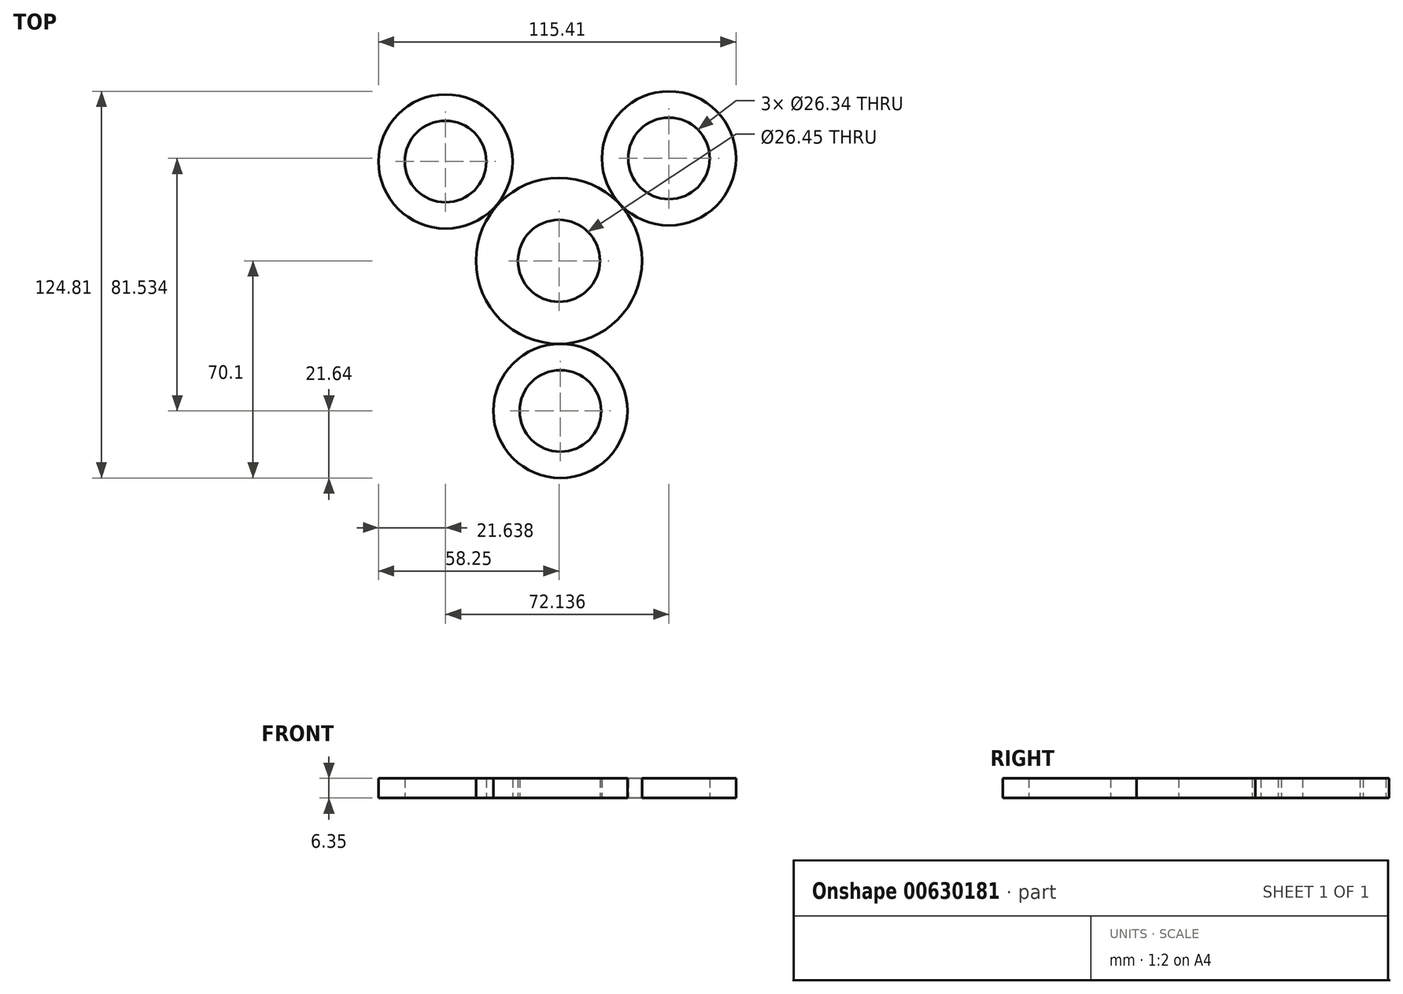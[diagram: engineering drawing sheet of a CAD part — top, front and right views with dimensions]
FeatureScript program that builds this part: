
annotation { "Feature Type Name" : "Feature", "Feature Type Description" : "" }
export const myFeature = defineFeature(function(context is Context, id is Id, definition is map)
    precondition{}
    {
        {
            var Q0;
            Q0=qCreatedBy(makeId("Top.planeOp"),FACE);
            var sketch = newSketch(context, id + "F0", { "sketchPlane" : qUnion([Q0])});
            skCircle(sketch, "E0", {"center": v(0, 0) * mm, "radius": 13.23 * mm});
            skSolve(sketch);
        }
        {
            var Q0;
            Q0=makeQuery(id+"F0.imprint","IMPRINT",FACE,{"disambiguationData":[TD([[makeQuery(id+"F0.imprint","IMPRINT",EDGE,{"derivedFrom":sQuery(id+"F0.wireOp",EDGE,"E0")}),1.0]])]});
            var sketch = newSketch(context, id + "F1", { "sketchPlane" : qUnion([Q0])});
            skCircle(sketch, "E1", {"center": v(0, 0) * mm, "radius": 26.8 * mm});
            skSolve(sketch);
        }
        {
            var Q0;
            Q0=makeQuery(id+"F1.imprint","IMPRINT",FACE,{"disambiguationData":[TD([[makeQuery(id+"F1.imprint","IMPRINT",EDGE,{"derivedFrom":sQuery(id+"F1.wireOp",EDGE,"E1")}),1.0]])]});
            extrude(context, id + "F2", {"entities" : qUnion([Q0]), "depth" : 6.35 * mm, "offsetDistance" : 25.4 * mm});
        }
        {
            var Q0;
            Q0=qCreatedBy(makeId("Top.planeOp"),FACE);
            var sketch = newSketch(context, id + "F3", { "sketchPlane" : qUnion([Q0])});
            skCircle(sketch, "E2", {"center": v(-36.61, 32.06) * mm, "radius": 21.64 * mm});
            skCircle(sketch, "E3", {"center": v(-36.61, 32.06) * mm, "radius": 13.17 * mm});
            skSolve(sketch);
        }
        {
            var Q0;
            Q0=makeQuery(id+"F3.imprint","IMPRINT",FACE,{"disambiguationData":[TD([[makeQuery(id+"F3.imprint","IMPRINT",EDGE,{"derivedFrom":sQuery(id+"F3.wireOp",EDGE,"E2")}),1.0]])]});
            extrude(context, id + "F4", {"entities" : qUnion([Q0]), "depth" : 6.35 * mm, "offsetDistance" : 25.4 * mm});
        }
        {
            var Q0;
            Q0=makeQuery(id+"F4.opExtrude","SWEPT_BODY",BODY,{"disambiguationData":[OSD([sQuery(id+"F3.wireOp",EDGE,"E2"),sQuery(id+"F3.wireOp",EDGE,"E3")])]});
            transform(context, id + "F5", {"entities" : qUnion([Q0]), "transformType" : TransformType.TRANSLATION_3D, "dx" : 0 * mm, "dy" : 0 * mm, "dz" : 0 * mm, "makeCopy" : true});
        }
        {
            var Q0;
            Q0=makeQuery(id+"F5.opPattern","COPY",BODY,{"derivedFrom":makeQuery(id+"F4.opExtrude","SWEPT_BODY",BODY,{"disambiguationData":[OSD([sQuery(id+"F3.wireOp",EDGE,"E2"),sQuery(id+"F3.wireOp",EDGE,"E3")])]}),"instanceName":"1"});
            deleteBodies(context, id + "F6", {"entities" : qUnion([Q0])});
        }
        {
            var Q0;
            Q0=makeQuery(id+"F4.opExtrude","SWEPT_BODY",BODY,{"disambiguationData":[OSD([sQuery(id+"F3.wireOp",EDGE,"E2"),sQuery(id+"F3.wireOp",EDGE,"E3")])]});
            transform(context, id + "F7", {"entities" : qUnion([Q0]), "transformType" : TransformType.TRANSLATION_3D, "dx" : 72.14 * mm, "dy" : 1.02 * mm, "dz" : 0 * mm, "makeCopy" : true});
        }
        {
            var Q0;
            Q0=makeQuery(id+"F4.opExtrude","SWEPT_BODY",BODY,{"disambiguationData":[OSD([sQuery(id+"F3.wireOp",EDGE,"E2"),sQuery(id+"F3.wireOp",EDGE,"E3")])]});
            transform(context, id + "F8", {"entities" : qUnion([Q0]), "transformType" : TransformType.TRANSLATION_3D, "dx" : 37.08 * mm, "dy" : -80.52 * mm, "dz" : 0 * mm, "makeCopy" : true});
        }
    });
